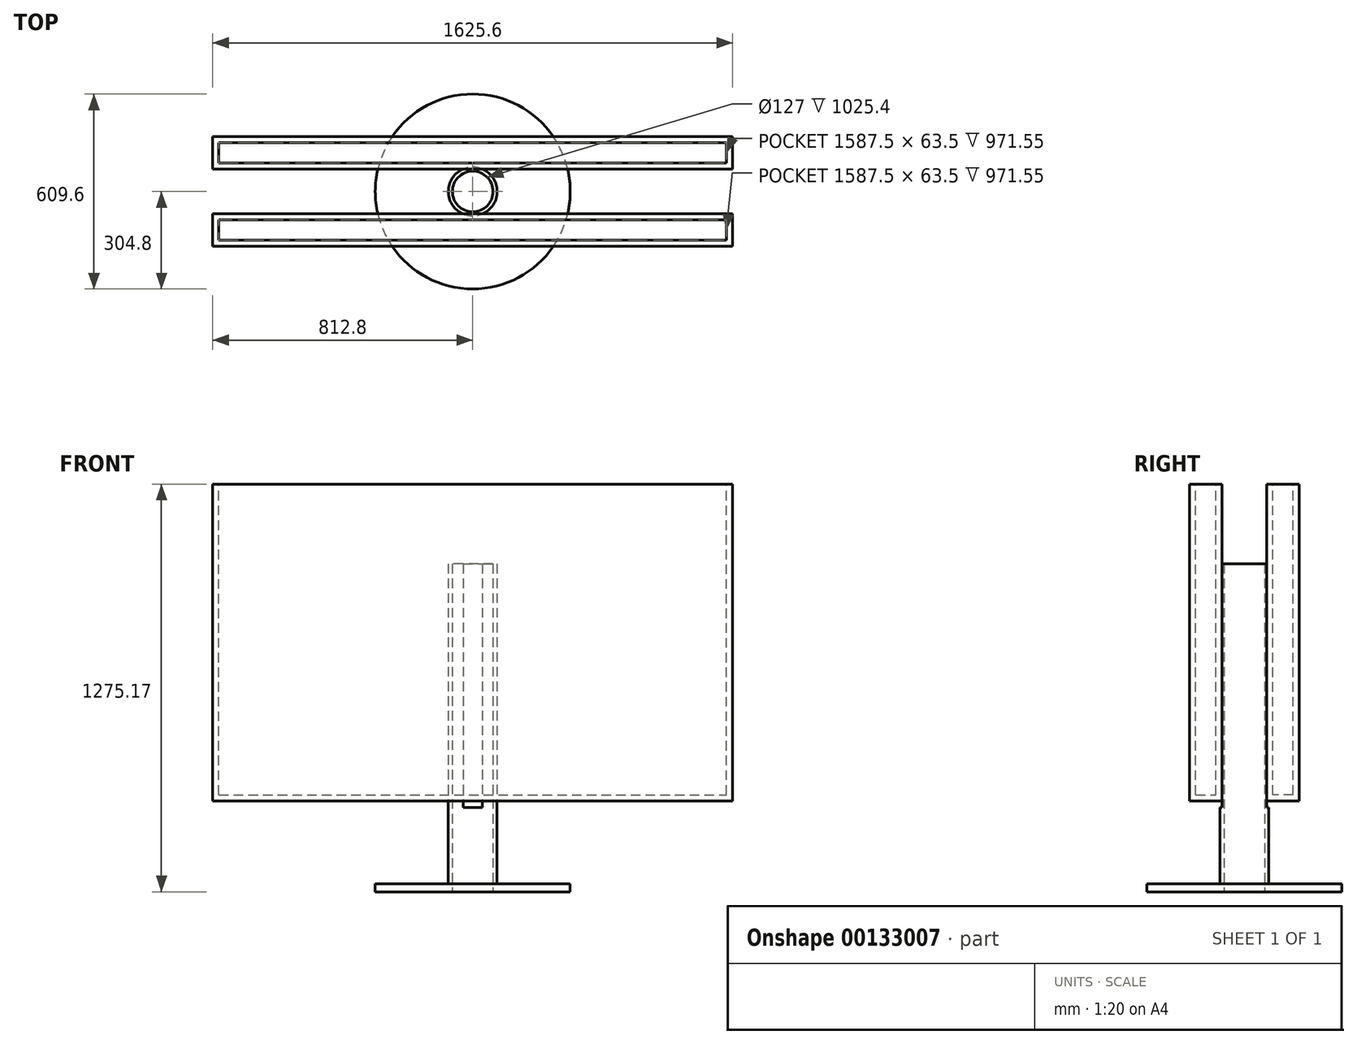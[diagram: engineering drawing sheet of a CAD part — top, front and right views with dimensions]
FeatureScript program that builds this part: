
annotation { "Feature Type Name" : "Feature", "Feature Type Description" : "" }
export const myFeature = defineFeature(function(context is Context, id is Id, definition is map)
    precondition{}
    {
        {
            var Q0;
            Q0=qCreatedBy(makeId("Top.planeOp"),FACE);
            var sketch = newSketch(context, id + "F0", { "sketchPlane" : qUnion([Q0])});
            skCircle(sketch, "E0", {"center": v(0, 0) * mm, "radius": 304.8 * mm});
            skSolve(sketch);
        }
        {
            var Q0;
            Q0=makeQuery(id+"F0.imprint","IMPRINT",FACE,{"disambiguationData":[TD([[makeQuery(id+"F0.imprint","IMPRINT",EDGE,{"derivedFrom":sQuery(id+"F0.wireOp",EDGE,"E0")}),1.0]])]});
            extrude(context, id + "F1", {"entities" : qUnion([Q0]), "depth" : 25.4 * mm});
        }
        {
            var Q0;
            Q0=makeQuery(id+"F1.opExtrude","CAP_FACE",FACE,{"disambiguationData":[OSD([sQuery(id+"F0.wireOp",EDGE,"E0")])],"isStart":false});
            var sketch = newSketch(context, id + "F2", { "sketchPlane" : qUnion([Q0])});
            skCircle(sketch, "E1", {"center": v(0, 0) * mm, "radius": 76.2 * mm});
            skCircle(sketch, "E2", {"center": v(0, 0) * mm, "radius": 63.5 * mm});
            skSolve(sketch);
        }
        {
            var Q0;
            Q0=makeQuery(id+"F2.imprint","IMPRINT",FACE,{"disambiguationData":[TD([[makeQuery(id+"F2.imprint","IMPRINT",EDGE,{"derivedFrom":sQuery(id+"F2.wireOp",EDGE,"E1")}),1.0]])]});
            extrude(context, id + "F3", {"entities" : qUnion([Q0]), "operationType" : NewBodyOperationType.ADD, "depth" : 1000 * mm});
        }
        {
            var Q0;
            Q0=makeQuery(id+"F3.boolean.opBoolean","SPLIT",FACE,{"disambiguationData":[TD([makeQuery(id+"F3.opExtrude","SWEPT_FACE",FACE,{"disambiguationData":[OSD([sQuery(id+"F2.wireOp",EDGE,"E2")])]})])],"derivedFrom":makeQuery(id+"F1.opExtrude","CAP_FACE",FACE,{"disambiguationData":[OSD([sQuery(id+"F0.wireOp",EDGE,"E0")])],"isStart":false})});
            extrude(context, id + "F4", {"entities" : qUnion([Q0]), "operationType" : NewBodyOperationType.REMOVE, "oppositeDirection" : true, "depth" : 25.4 * mm});
        }
        {
            var Q0;
            Q0=makeQuery(id+"F3.opExtrude","CAP_FACE",FACE,{"disambiguationData":[OSD([sQuery(id+"F2.wireOp",EDGE,"E1"),sQuery(id+"F2.wireOp",EDGE,"E2")])],"isStart":false});
            var sketch = newSketch(context, id + "F5", { "sketchPlane" : qUnion([Q0])});
            skLineSegment(sketch, "E3.bottom", {"start": v(-76.06, -69.85) * mm, "end": v(76.06, -69.85) * mm});
            skLineSegment(sketch, "E3.top", {"start": v(-76.06, -98.99) * mm, "end": v(76.06, -98.99) * mm});
            skLineSegment(sketch, "E3.left", {"start": v(-76.06, -69.85) * mm, "end": v(-76.06, -98.99) * mm});
            skLineSegment(sketch, "E3.right", {"start": v(76.06, -69.85) * mm, "end": v(76.06, -98.99) * mm});
            skPoint(sketch, "E3.middle", {"position": v(0, -84.42) * mm});
            skLineSegment(sketch, "E4.bottom", {"start": v(-80.78, 69.85) * mm, "end": v(80.78, 69.85) * mm});
            skLineSegment(sketch, "E4.top", {"start": v(-80.78, 104.99) * mm, "end": v(80.78, 104.99) * mm});
            skLineSegment(sketch, "E4.left", {"start": v(-80.78, 69.85) * mm, "end": v(-80.78, 104.99) * mm});
            skLineSegment(sketch, "E4.right", {"start": v(80.78, 69.85) * mm, "end": v(80.78, 104.99) * mm});
            skPoint(sketch, "E4.middle", {"position": v(0, 87.42) * mm});
            skSolve(sketch);
        }
        {
            var Q0;
            Q0 = qSketchRegion(id + "F5", true);
            extrude(context, id + "F6", {"entities" : qUnion([Q0]), "operationType" : NewBodyOperationType.REMOVE, "oppositeDirection" : true, "depth" : 762 * mm});
        }
        {
            var Q0;
            Q0=makeQuery(id+"F6.boolean.opBoolean","COPY",FACE,{"derivedFrom":makeQuery(id+"F6.opExtrude","SWEPT_FACE",FACE,{"disambiguationData":[OSD([sQuery(id+"F5.wireOp",EDGE,"E4.bottom")])]})});
            var sketch = newSketch(context, id + "F7", { "sketchPlane" : qUnion([Q0])});
            skLineSegment(sketch, "E5.bottom", {"start": v(812.8, 284.57) * mm, "end": v(-812.8, 284.57) * mm});
            skLineSegment(sketch, "E5.top", {"start": v(812.8, 1275.17) * mm, "end": v(-812.8, 1275.17) * mm});
            skLineSegment(sketch, "E5.left", {"start": v(812.8, 284.57) * mm, "end": v(812.8, 1275.17) * mm});
            skLineSegment(sketch, "E5.right", {"start": v(-812.8, 284.57) * mm, "end": v(-812.8, 1275.17) * mm});
            skPoint(sketch, "E5.middle", {"position": v(0, 779.87) * mm});
            skSolve(sketch);
        }
        {
            var Q0;
            Q0 = qSketchRegion(id + "F7", true);
            extrude(context, id + "F8", {"entities" : qUnion([Q0]), "depth" : 101.6 * mm});
        }
        {
            var Q0;
            Q0=makeQuery(id+"F8.opExtrude","SWEPT_FACE",FACE,{"disambiguationData":[OSD([sQuery(id+"F7.wireOp",EDGE,"E5.top")])]});
            shell(context, id + "F9", {"entities" : qUnion([Q0]), "thickness" : 19.05 * mm});
        }
        {
            var Q0;
            Q0=makeQuery(id+"F8.opExtrude","SWEPT_BODY",BODY,{"disambiguationData":[OSD([sQuery(id+"F7.wireOp",EDGE,"E5.bottom"),sQuery(id+"F7.wireOp",EDGE,"E5.top"),sQuery(id+"F7.wireOp",EDGE,"E5.left"),sQuery(id+"F7.wireOp",EDGE,"E5.right")])]});
            var Q1;
            Q1=qCreatedBy(makeId("Front.planeOp"),FACE);
            mirror(context, id + "F10", {"entities" : qUnion([Q0]), "mirrorPlane" : qUnion([Q1])});
        }
    });
